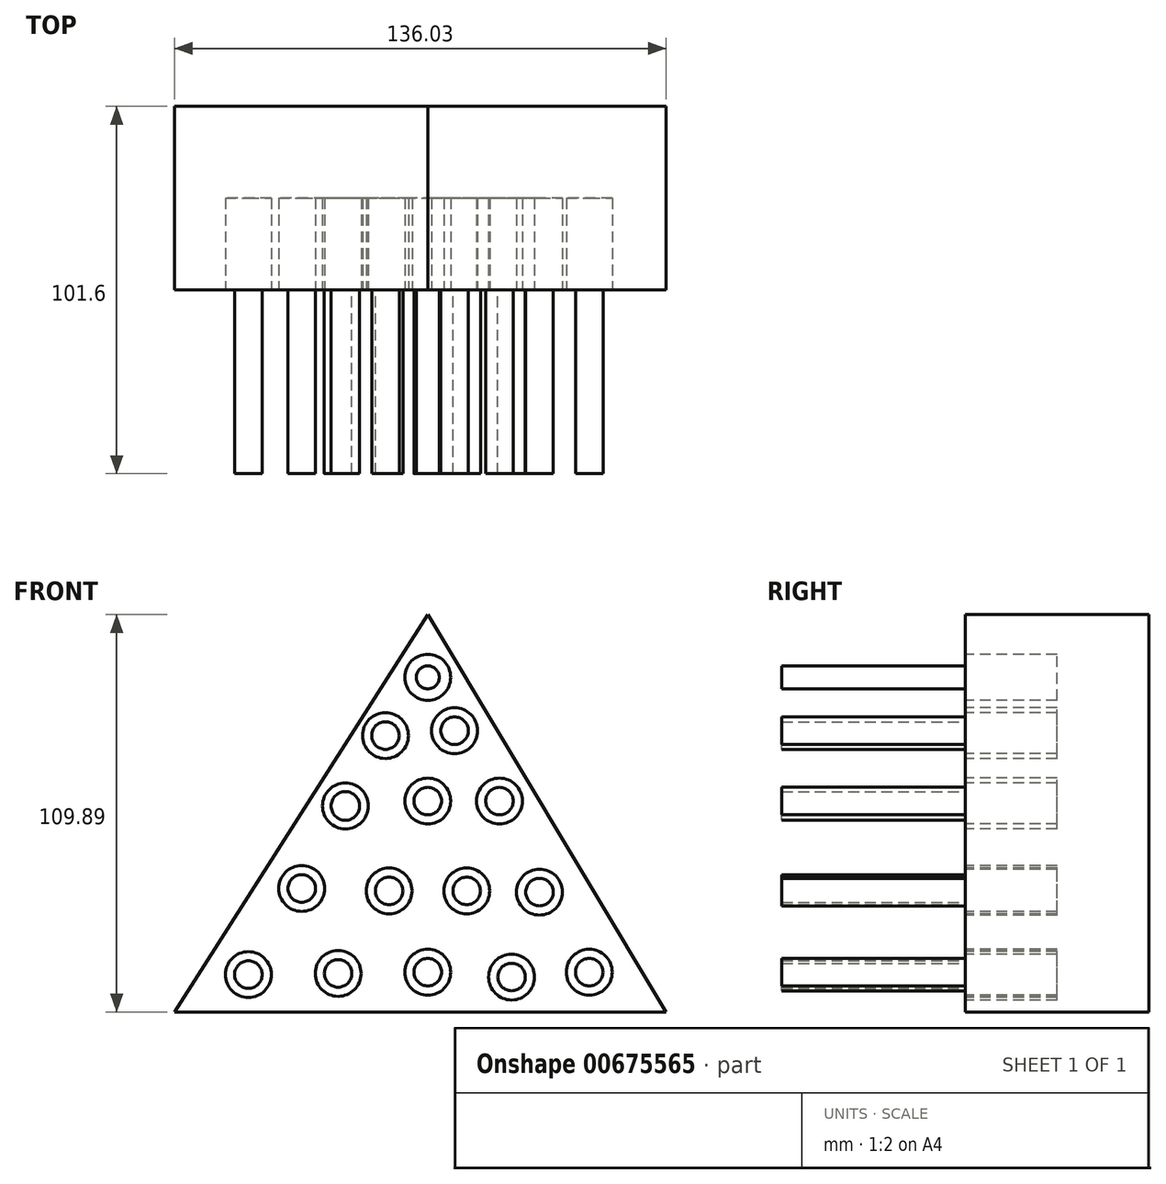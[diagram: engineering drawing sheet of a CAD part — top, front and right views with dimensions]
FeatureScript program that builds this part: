
annotation { "Feature Type Name" : "Feature", "Feature Type Description" : "" }
export const myFeature = defineFeature(function(context is Context, id is Id, definition is map)
    precondition{}
    {
        {
            var Q0;
            Q0=qCreatedBy(makeId("Front.planeOp"),FACE);
            var sketch = newSketch(context, id + "F0", { "sketchPlane" : qUnion([Q0])});
            skLineSegment(sketch, "E0", {"start": v(0, 73.23) * mm, "end": v(-70.08, -36.66) * mm});
            skLineSegment(sketch, "E1", {"start": v(-70.08, -36.66) * mm, "end": v(65.95, -36.66) * mm});
            skLineSegment(sketch, "E2", {"start": v(65.95, -36.66) * mm, "end": v(0, 73.23) * mm});
            skSolve(sketch);
        }
        {
            var Q0;
            Q0 = qSketchRegion(id + "F0", true);
            extrude(context, id + "F1", {"entities" : qUnion([Q0]), "depth" : 50.8 * mm, "offsetDistance" : 25.4 * mm});
        }
        {
            var Q0;
            Q0=makeQuery(id+"F1.opExtrude","CAP_FACE",FACE,{"disambiguationData":[OSD([sQuery(id+"F0.wireOp",EDGE,"E0"),sQuery(id+"F0.wireOp",EDGE,"E1"),sQuery(id+"F0.wireOp",EDGE,"E2")])],"isStart":false});
            var sketch = newSketch(context, id + "F2", { "sketchPlane" : qUnion([Q0])});
            skCircle(sketch, "E3", {"center": v(-49.64, -26.34) * mm, "radius": 6.35 * mm});
            skCircle(sketch, "E4", {"center": v(-24.8, -26) * mm, "radius": 6.35 * mm});
            skCircle(sketch, "E5", {"center": v(0, -25.67) * mm, "radius": 6.35 * mm});
            skCircle(sketch, "E6", {"center": v(23.2, -27.01) * mm, "radius": 6.35 * mm});
            skCircle(sketch, "E7", {"center": v(44.68, -25.67) * mm, "radius": 6.35 * mm});
            skSolve(sketch);
        }
        {
            var Q0;
            Q0 = qSketchRegion(id + "F2", true);
            extrude(context, id + "F3", {"entities" : qUnion([Q0]), "operationType" : NewBodyOperationType.REMOVE, "oppositeDirection" : true, "depth" : 25.4 * mm, "offsetDistance" : 25.4 * mm});
        }
        {
            var Q0;
            Q0=makeQuery(id+"F1.opExtrude","CAP_FACE",FACE,{"disambiguationData":[OSD([sQuery(id+"F0.wireOp",EDGE,"E0"),sQuery(id+"F0.wireOp",EDGE,"E1"),sQuery(id+"F0.wireOp",EDGE,"E2")])],"isStart":false});
            var sketch = newSketch(context, id + "F4", { "sketchPlane" : qUnion([Q0])});
            skCircle(sketch, "E8", {"center": v(-34.87, -2.51) * mm, "radius": 6.35 * mm});
            skCircle(sketch, "E9", {"center": v(-10.7, -3.18) * mm, "radius": 6.35 * mm});
            skCircle(sketch, "E10", {"center": v(10.78, -3.18) * mm, "radius": 6.35 * mm});
            skCircle(sketch, "E11", {"center": v(30.92, -3.52) * mm, "radius": 6.35 * mm});
            skSolve(sketch);
        }
        {
            var Q0;
            Q0 = qSketchRegion(id + "F4", true);
            extrude(context, id + "F5", {"entities" : qUnion([Q0]), "operationType" : NewBodyOperationType.REMOVE, "oppositeDirection" : true, "depth" : 25.4 * mm, "offsetDistance" : 25.4 * mm});
        }
        {
            var Q0;
            Q0=makeQuery(id+"F1.opExtrude","CAP_FACE",FACE,{"disambiguationData":[OSD([sQuery(id+"F0.wireOp",EDGE,"E0"),sQuery(id+"F0.wireOp",EDGE,"E1"),sQuery(id+"F0.wireOp",EDGE,"E2")])],"isStart":false});
            var sketch = newSketch(context, id + "F6", { "sketchPlane" : qUnion([Q0])});
            skCircle(sketch, "E12", {"center": v(-22.78, 20.31) * mm, "radius": 6.35 * mm});
            skCircle(sketch, "E13", {"center": v(0, 21.66) * mm, "radius": 6.35 * mm});
            skCircle(sketch, "E14", {"center": v(19.85, 21.66) * mm, "radius": 6.35 * mm});
            skSolve(sketch);
        }
        {
            var Q0;
            Q0 = qSketchRegion(id + "F6", true);
            extrude(context, id + "F7", {"entities" : qUnion([Q0]), "operationType" : NewBodyOperationType.REMOVE, "oppositeDirection" : true, "depth" : 25.4 * mm, "offsetDistance" : 25.4 * mm});
        }
        {
            var Q0;
            Q0=makeQuery(id+"F1.opExtrude","CAP_FACE",FACE,{"disambiguationData":[OSD([sQuery(id+"F0.wireOp",EDGE,"E0"),sQuery(id+"F0.wireOp",EDGE,"E1"),sQuery(id+"F0.wireOp",EDGE,"E2")])],"isStart":false});
            var sketch = newSketch(context, id + "F8", { "sketchPlane" : qUnion([Q0])});
            skCircle(sketch, "E15", {"center": v(-11.7, 39.78) * mm, "radius": 6.35 * mm});
            skCircle(sketch, "E16", {"center": v(7.43, 41.13) * mm, "radius": 6.35 * mm});
            skCircle(sketch, "E17", {"center": v(0, 55.9) * mm, "radius": 6.35 * mm});
            skSolve(sketch);
        }
        {
            var Q0;
            Q0 = qSketchRegion(id + "F8", true);
            extrude(context, id + "F9", {"entities" : qUnion([Q0]), "operationType" : NewBodyOperationType.REMOVE, "oppositeDirection" : true, "depth" : 25.4 * mm, "offsetDistance" : 25.4 * mm});
        }
        {
            var Q0;
            Q0=makeQuery(id+"F1.opExtrude","CAP_FACE",FACE,{"disambiguationData":[OSD([sQuery(id+"F0.wireOp",EDGE,"E0"),sQuery(id+"F0.wireOp",EDGE,"E1"),sQuery(id+"F0.wireOp",EDGE,"E2")])],"isStart":false});
            var sketch = newSketch(context, id + "F10", { "sketchPlane" : qUnion([Q0])});
            skCircle(sketch, "E18", {"center": v(0, 55.9) * mm, "radius": 3.18 * mm});
            skSolve(sketch);
        }
        {
            var Q0;
            Q0 = qSketchRegion(id + "F10", true);
            extrude(context, id + "F11", {"entities" : qUnion([Q0]), "depth" : 50.8 * mm, "offsetDistance" : 25.4 * mm});
        }
        {
            var Q0;
            Q0=makeQuery(id+"F1.opExtrude","CAP_FACE",FACE,{"disambiguationData":[OSD([sQuery(id+"F0.wireOp",EDGE,"E0"),sQuery(id+"F0.wireOp",EDGE,"E1"),sQuery(id+"F0.wireOp",EDGE,"E2")])],"isStart":false});
            var sketch = newSketch(context, id + "F12", { "sketchPlane" : qUnion([Q0])});
            skCircle(sketch, "E19", {"center": v(-11.7, 39.78) * mm, "radius": 3.81 * mm});
            skCircle(sketch, "E20", {"center": v(7.43, 41.13) * mm, "radius": 3.81 * mm});
            skSolve(sketch);
        }
        {
            var Q0;
            Q0 = qSketchRegion(id + "F12", true);
            extrude(context, id + "F13", {"entities" : qUnion([Q0]), "depth" : 50.8 * mm, "offsetDistance" : 25.4 * mm});
        }
        {
            var Q0;
            Q0=makeQuery(id+"F1.opExtrude","CAP_FACE",FACE,{"disambiguationData":[OSD([sQuery(id+"F0.wireOp",EDGE,"E0"),sQuery(id+"F0.wireOp",EDGE,"E1"),sQuery(id+"F0.wireOp",EDGE,"E2")])],"isStart":false});
            var sketch = newSketch(context, id + "F14", { "sketchPlane" : qUnion([Q0])});
            skCircle(sketch, "E21", {"center": v(0, 21.66) * mm, "radius": 3.81 * mm});
            skCircle(sketch, "E22", {"center": v(19.85, 21.66) * mm, "radius": 3.81 * mm});
            skCircle(sketch, "E23", {"center": v(-22.78, 20.31) * mm, "radius": 3.96 * mm});
            skSolve(sketch);
        }
        {
            var Q0;
            Q0 = qSketchRegion(id + "F14", true);
            extrude(context, id + "F15", {"entities" : qUnion([Q0]), "depth" : 50.8 * mm, "offsetDistance" : 25.4 * mm});
        }
        {
            var Q0;
            Q0=makeQuery(id+"F1.opExtrude","CAP_FACE",FACE,{"disambiguationData":[OSD([sQuery(id+"F0.wireOp",EDGE,"E0"),sQuery(id+"F0.wireOp",EDGE,"E1"),sQuery(id+"F0.wireOp",EDGE,"E2")])],"isStart":false});
            var sketch = newSketch(context, id + "F16", { "sketchPlane" : qUnion([Q0])});
            skCircle(sketch, "E24", {"center": v(-49.64, -26.34) * mm, "radius": 3.81 * mm});
            skCircle(sketch, "E25", {"center": v(-24.8, -26) * mm, "radius": 3.81 * mm});
            skCircle(sketch, "E26", {"center": v(0, -25.67) * mm, "radius": 3.81 * mm});
            skCircle(sketch, "E27", {"center": v(23.2, -27.01) * mm, "radius": 3.81 * mm});
            skCircle(sketch, "E28", {"center": v(44.68, -25.67) * mm, "radius": 3.81 * mm});
            skCircle(sketch, "E29", {"center": v(-34.87, -2.51) * mm, "radius": 3.81 * mm});
            skCircle(sketch, "E30", {"center": v(-10.7, -3.18) * mm, "radius": 3.81 * mm});
            skCircle(sketch, "E31", {"center": v(10.78, -3.18) * mm, "radius": 3.81 * mm});
            skCircle(sketch, "E32", {"center": v(30.92, -3.52) * mm, "radius": 3.81 * mm});
            skSolve(sketch);
        }
        {
            var Q0;
            Q0 = qSketchRegion(id + "F16", true);
            extrude(context, id + "F17", {"entities" : qUnion([Q0]), "depth" : 50.8 * mm, "offsetDistance" : 25.4 * mm});
        }
    });
